# Revit family: Flash EN 54-23_Aguilera Electronica
name_source: partatom
category: Dispositivos de alarma de incendios
revit_build: Autodesk Revit 2017 (Build: 20160225_1515(x64)
units: mm (PartAtom-declared; Revit-internal decimal feet)

## family parameters
Anfitrión = Cara
Compartido = No
Corte con vacíos al cargar = No
Cota de conector redondo = Diámetro de uso
Mantener orientación de anotación = Sí
Número OmniClass = 23.85.30.21.11.11.11
Punto de cálculo de habitación = No
Tipo de pieza = Normal
Título OmniClass = Smoke Detectors

## types (4) — shared parameters
Altura 1 = 38 mm  [stored 0.124672 ft]
Altura 3 = 8 mm  [stored 0.0262467 ft]
Diámetro = 93 mm  [stored 0.305118 ft]
Elevación por defecto = 1200 mm
Fabricante = Aguilera Electrónica
Radio = 47 mm
Símbolo = Sí
Símbolo texto modelo = Sí
URL = https://aguilera.es

## per-type parameters (varying)
| type | Altura 2 | Carcasa | Comentarios de tipo | Descripción | Modelo | Suplemento para superficie |
| Flash EN 54-23 para montaje en techo base baja | 1 mm  [stored 0.00328084 ft] | Carcasa ABS | Flash certificado EN 54-23 para montaje en techo. Tipo C-3-7.5. Máxima altura de instalación 3m, longitud de cobertura 7.5 m. Tecnología led que garantiza una intensidad luminosa 0.4lux/m2 en todo el área. Frecuencia de flash seleccionable entre 1Hz y 0.5Hz Consumo máximo 25mA. Protección IP33 con base baja, IP65 con base alta. | Flash certificado EN 54-23 para montaje en techo.Con un diseño de lente único que distribuye la luz de forma cilíndrica para alcanzar la iluminación requerida por la norma EN 54-23. Tecnología de led que garantiza una intensidad luminosa 0.4 lux/m2 en toda el área. Diseñado para la instalación en una altura de hasta 3m y con un aspecto discreto. Este dispositivo es ideal para una variedad de usos, incluyendo dormitorios, cuartos de baño y aseos. | AE/V-AFLXC | No |
| Flash EN 54-23 para montaje en techo base alta | 28 mm  [stored 0.0918635 ft] | Carcasa ABS | Flash certificado EN 54-23 para montaje en techo. Tipo C-3-7.5. Máxima altura de instalación 3m, longitud de cobertura 7.5 m. Tecnología led que garantiza una intensidad luminosa 0.4lux/m2 en todo el área. Frecuencia de flash seleccionable entre 1Hz y 0.5Hz Consumo máximo 25mA. Protección IP33 con base baja, IP65 con base alta. | Flash certificado EN 54-23 para montaje en techo.Con un diseño de lente único que distribuye la luz de forma cilíndrica para alcanzar la iluminación requerida por la norma EN 54-23. Tecnología de led que garantiza una intensidad luminosa 0.4 lux/m2 en toda el área. Diseñado para la instalación en una altura de hasta 3m y con un aspecto discreto. Este dispositivo es ideal para una variedad de usos, incluyendo dormitorios, cuartos de baño y aseos. | AE/V-AFLXC1 | Sí |
| Flash EN 54-23 para montaje en pared base alta | 28 mm  [stored 0.0918635 ft] | Carcasa ABS rojo | Flash certificado EN 54-23 para montaje en pared. Tipo W-2.4-7.5. Máxima altura de instalación 2.4m, longitud de cobertura 7.5 m. Tecnología led que garantiza una intensidad luminosa 0.4lux/m2 en todo el área. Frecuencia de flash seleccionable entre 1Hz y 0.5Hz Consumo máximo 25mA. Protección IP33 con base baja, IP65 con base alta. | Flash certificado EN 54-23 para montaje en pared.Tecnológia led que
garantiza intensidad luminosa. | AE/V-AFLXW1 | Sí |
| Flash EN 54-23 para montaje en pared base baja | 1 mm  [stored 0.00328084 ft] | Carcasa ABS rojo | Flash certificado EN 54-23 para montaje en pared. Tipo W-2.4-7.5. Máxima altura de instalación 2.4m, longitud de cobertura 7.5 m. Tecnología led que garantiza una intensidad luminosa 0.4lux/m2 en todo el área. Frecuencia de flash seleccionable entre 1Hz y 0.5Hz Consumo máximo 25mA. Protección IP33 con base baja, IP65 con base alta. | Flash certificado EN 54-23 para montaje en pared.Tecnológia led que
garantiza intensidad luminosa. | AE/V-AFLXW | Sí |

note: [stored X ft] marks values corroborated as IEEE doubles in the binary element streams (Revit-internal decimal feet)
